# Revit family: Comfort_Window_F_Side_Hung_Custom
name_source: partatom
category: Windows
revit_build: Autodesk Revit 2014 (Build: 20130308_1515(x64)
units: mm (PartAtom-declared; Revit-internal decimal feet)

## types (1)
- Comfort-TypeF-Side-Custom
    Clearvue SHGC Value = 1
    Clearvue U Value = 1
    DG Gasket Thickness = 12 mm  [stored 0.0393701 ft]
    Description = Comfort Window, Side Hung, Type F
    Double Glazing Gasket Finish = Double Glazing Gasket Material
    Energy Advantage SHGC Value = 1
    Energy Advantage U Value = 1
    Frame Depth = 33 mm  [stored 0.108268 ft]
    Frame Edge Thickness = 26 mm
    Intruderprufe LowE SHGC Value = 1
    Intruderprufe LowE U Value = 1
    Intruderprufe SHGC Value = 1
    Intruderprufe U Value = 1
    Limit Fixed Pane Height Max = 1800 mm  [stored 5.90551 ft]
    Limit Fixed Pane Height Min = 200 mm  [stored 0.656168 ft]
    Limit Fixed Pane Width Max = 1800 mm  [stored 5.90551 ft]
    Limit Fixed Pane Width Min = 200 mm  [stored 0.656168 ft]
    Limit Sash Height Max = 1200 mm
    Limit Sash Height Min = 300 mm  [stored 0.984252 ft]
    Limit Sash Width Max = 600 mm  [stored 1.9685 ft]
    Limit Sash Width Min = 300 mm  [stored 0.984252 ft]
    Limit Window Height Max = 1852 mm
    Manufacturer = Crealco
    Max System DG One Piece Thickness = 4 mm  [stored 0.0131234 ft]
    Max System DG Unit Thickness = 20 mm  [stored 0.0656168 ft]
    Model = Comfort Window
    Mullion Width = 27 mm  [stored 0.0885827 ft]
    Rough Height = 590 mm  [stored 1.9357 ft]
    Rough Width = 902 mm  [stored 2.95932 ft]
    Sash Frame Gap = 5 mm  [stored 0.0164042 ft]
    Sash Frame Side Gap = 12 mm  [stored 0.0393701 ft]
    Sash Side Gap = 38 mm
    SmartGlass Elite SHGC Value = 1
    SmartGlass Elite U Value = 1
    SmartGlass Plus SHGC Value = 1
    SmartGlass Plus U Value = 1
    SmartGlass Standard SHGC Value = 1
    SmartGlass Standard U Value = 1
    SmartGlass Superior SHGC Value = 1
    SmartGlass Superior U Value = 1
    Transom Height = 27 mm  [stored 0.0885827 ft]
    URL = http://www.crealco.co.za
    Visual Light Transmittance = 0

note: [stored X ft] marks values corroborated as IEEE doubles in the binary element streams (Revit-internal decimal feet)

## geometry (parser evidence)
native form markers: Sweep x17
no freeform markers — native parametric forms only
